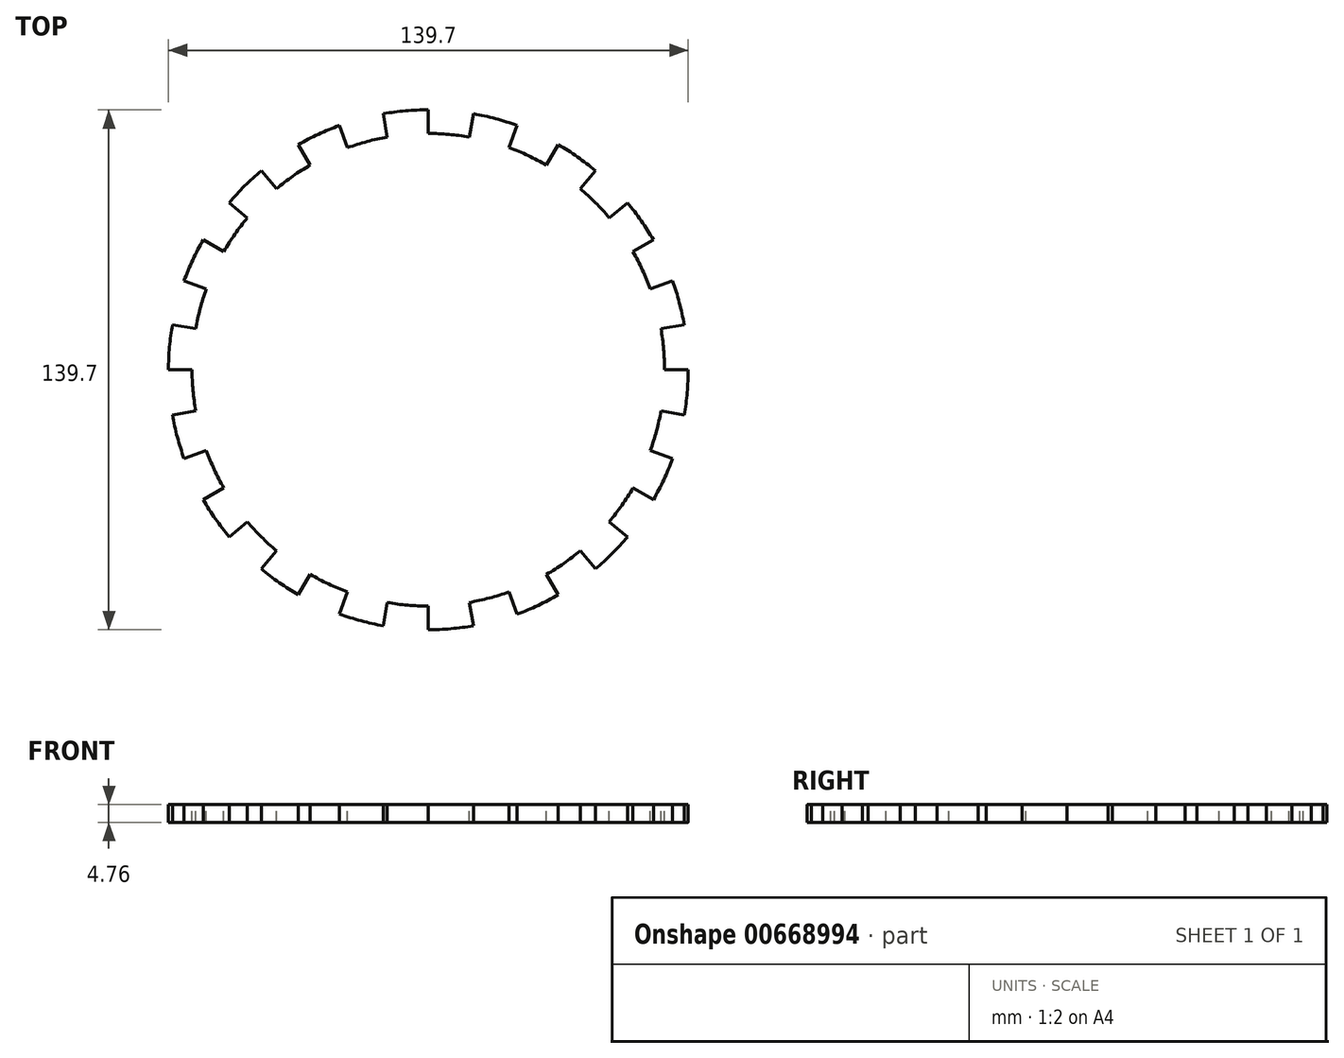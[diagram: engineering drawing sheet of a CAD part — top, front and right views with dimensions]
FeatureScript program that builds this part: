
annotation { "Feature Type Name" : "Feature", "Feature Type Description" : "" }
export const myFeature = defineFeature(function(context is Context, id is Id, definition is map)
    precondition{}
    {
        {
            var Q0;
            Q0=qCreatedBy(makeId("Top.planeOp"),FACE);
            var sketch = newSketch(context, id + "F0", { "sketchPlane" : qUnion([Q0])});
            skCircle(sketch, "E0", {"center": v(0, 0) * mm, "radius": 69.85 * mm});
            skSolve(sketch);
        }
        {
            var Q0;
            Q0 = qSketchRegion(id + "F0", true);
            extrude(context, id + "F1", {"entities" : qUnion([Q0]), "depth" : 4.76 * mm, "offsetDistance" : 25.4 * mm});
        }
        {
            var Q0;
            Q0=makeQuery(id+"F1.opExtrude","CAP_FACE",FACE,{"disambiguationData":[OSD([sQuery(id+"F0.wireOp",EDGE,"E0")])],"isStart":false});
            var sketch = newSketch(context, id + "F2", { "sketchPlane" : qUnion([Q0])});
            skLineSegment(sketch, "E1", {"start": v(0, 69.85) * mm, "end": v(0, 63.5) * mm});
            skLineSegment(sketch, "E2", {"start": v(12.13, 68.79) * mm, "end": v(11.03, 62.54) * mm});
            skArc(sketch, "E3", {"start": v(0, 63.5) * mm, "mid": v(5.53, 63.26) * mm, "end": v(11.03, 62.54) * mm});
            skArc(sketch, "E4", {"start": v(0, 69.85) * mm, "mid": v(6.09, 69.58) * mm, "end": v(12.13, 68.79) * mm});
            skArc(sketch, "E5.1.0", {"start": v(-23.9, 65.64) * mm, "mid": v(-18.08, 67.47) * mm, "end": v(-12.13, 68.79) * mm});
            skLineSegment(sketch, "E5.1.1", {"start": v(-12.13, 68.79) * mm, "end": v(-11.03, 62.54) * mm});
            skArc(sketch, "E5.1.2", {"start": v(-21.72, 59.67) * mm, "mid": v(-16.44, 61.34) * mm, "end": v(-11.03, 62.54) * mm});
            skLineSegment(sketch, "E5.1.3", {"start": v(-23.9, 65.64) * mm, "end": v(-21.72, 59.67) * mm});
            skArc(sketch, "E5.2.0", {"start": v(-44.9, 53.5) * mm, "mid": v(-40.06, 57.22) * mm, "end": v(-34.93, 60.5) * mm});
            skLineSegment(sketch, "E5.2.1", {"start": v(-34.93, 60.5) * mm, "end": v(-31.75, 55) * mm});
            skArc(sketch, "E5.2.2", {"start": v(-40.82, 48.64) * mm, "mid": v(-36.42, 52.02) * mm, "end": v(-31.75, 55) * mm});
            skLineSegment(sketch, "E5.2.3", {"start": v(-44.9, 53.5) * mm, "end": v(-40.82, 48.64) * mm});
            skArc(sketch, "E5.3.0", {"start": v(-60.5, 34.93) * mm, "mid": v(-57.22, 40.06) * mm, "end": v(-53.5, 44.9) * mm});
            skLineSegment(sketch, "E5.3.1", {"start": v(-53.5, 44.9) * mm, "end": v(-48.64, 40.82) * mm});
            skArc(sketch, "E5.3.2", {"start": v(-55, 31.75) * mm, "mid": v(-52.02, 36.42) * mm, "end": v(-48.64, 40.82) * mm});
            skLineSegment(sketch, "E5.3.3", {"start": v(-60.5, 34.93) * mm, "end": v(-55, 31.75) * mm});
            skArc(sketch, "E5.4.0", {"start": v(-68.79, 12.13) * mm, "mid": v(-67.47, 18.08) * mm, "end": v(-65.64, 23.9) * mm});
            skLineSegment(sketch, "E5.4.1", {"start": v(-65.64, 23.9) * mm, "end": v(-59.67, 21.72) * mm});
            skArc(sketch, "E5.4.2", {"start": v(-62.54, 11.03) * mm, "mid": v(-61.34, 16.44) * mm, "end": v(-59.67, 21.72) * mm});
            skLineSegment(sketch, "E5.4.3", {"start": v(-68.79, 12.13) * mm, "end": v(-62.54, 11.03) * mm});
            skArc(sketch, "E5.5.0", {"start": v(-68.79, -12.13) * mm, "mid": v(-69.58, -6.09) * mm, "end": v(-69.85, 0) * mm});
            skLineSegment(sketch, "E5.5.1", {"start": v(-69.85, 0) * mm, "end": v(-63.5, 0) * mm});
            skArc(sketch, "E5.5.2", {"start": v(-62.54, -11.03) * mm, "mid": v(-63.26, -5.53) * mm, "end": v(-63.5, 0) * mm});
            skLineSegment(sketch, "E5.5.3", {"start": v(-68.79, -12.13) * mm, "end": v(-62.54, -11.03) * mm});
            skArc(sketch, "E5.6.0", {"start": v(-60.5, -34.92) * mm, "mid": v(-63.3, -29.52) * mm, "end": v(-65.64, -23.9) * mm});
            skLineSegment(sketch, "E5.6.1", {"start": v(-65.64, -23.9) * mm, "end": v(-59.67, -21.72) * mm});
            skArc(sketch, "E5.6.2", {"start": v(-55, -31.75) * mm, "mid": v(-57.55, -26.84) * mm, "end": v(-59.67, -21.72) * mm});
            skLineSegment(sketch, "E5.6.3", {"start": v(-60.5, -34.92) * mm, "end": v(-55, -31.75) * mm});
            skArc(sketch, "E5.7.0", {"start": v(-44.9, -53.5) * mm, "mid": v(-49.4, -49.4) * mm, "end": v(-53.5, -44.9) * mm});
            skLineSegment(sketch, "E5.7.1", {"start": v(-53.5, -44.9) * mm, "end": v(-48.64, -40.82) * mm});
            skArc(sketch, "E5.7.2", {"start": v(-40.82, -48.64) * mm, "mid": v(-44.9, -44.9) * mm, "end": v(-48.64, -40.82) * mm});
            skLineSegment(sketch, "E5.7.3", {"start": v(-44.9, -53.5) * mm, "end": v(-40.82, -48.64) * mm});
            skArc(sketch, "E5.8.0", {"start": v(-23.9, -65.64) * mm, "mid": v(-29.52, -63.3) * mm, "end": v(-34.92, -60.5) * mm});
            skLineSegment(sketch, "E5.8.1", {"start": v(-34.93, -60.5) * mm, "end": v(-31.75, -55) * mm});
            skArc(sketch, "E5.8.2", {"start": v(-21.72, -59.67) * mm, "mid": v(-26.84, -57.55) * mm, "end": v(-31.75, -55) * mm});
            skLineSegment(sketch, "E5.8.3", {"start": v(-23.9, -65.64) * mm, "end": v(-21.72, -59.67) * mm});
            skArc(sketch, "E5.9.0", {"start": v(0, -69.85) * mm, "mid": v(-6.09, -69.58) * mm, "end": v(-12.13, -68.79) * mm});
            skLineSegment(sketch, "E5.9.1", {"start": v(-12.13, -68.79) * mm, "end": v(-11.03, -62.54) * mm});
            skArc(sketch, "E5.9.2", {"start": v(0, -63.5) * mm, "mid": v(-5.53, -63.26) * mm, "end": v(-11.03, -62.54) * mm});
            skLineSegment(sketch, "E5.9.3", {"start": v(0, -69.85) * mm, "end": v(0, -63.5) * mm});
            skArc(sketch, "E5.10.0", {"start": v(23.9, -65.64) * mm, "mid": v(18.08, -67.47) * mm, "end": v(12.13, -68.79) * mm});
            skLineSegment(sketch, "E5.10.1", {"start": v(12.13, -68.79) * mm, "end": v(11.03, -62.54) * mm});
            skArc(sketch, "E5.10.2", {"start": v(21.72, -59.67) * mm, "mid": v(16.44, -61.34) * mm, "end": v(11.03, -62.54) * mm});
            skLineSegment(sketch, "E5.10.3", {"start": v(23.9, -65.64) * mm, "end": v(21.72, -59.67) * mm});
            skArc(sketch, "E5.11.0", {"start": v(44.9, -53.5) * mm, "mid": v(40.06, -57.22) * mm, "end": v(34.92, -60.5) * mm});
            skLineSegment(sketch, "E5.11.1", {"start": v(34.92, -60.5) * mm, "end": v(31.75, -55) * mm});
            skArc(sketch, "E5.11.2", {"start": v(40.82, -48.64) * mm, "mid": v(36.42, -52.02) * mm, "end": v(31.75, -55) * mm});
            skLineSegment(sketch, "E5.11.3", {"start": v(44.9, -53.5) * mm, "end": v(40.82, -48.64) * mm});
            skArc(sketch, "E5.12.0", {"start": v(60.5, -34.93) * mm, "mid": v(57.22, -40.06) * mm, "end": v(53.5, -44.9) * mm});
            skLineSegment(sketch, "E5.12.1", {"start": v(53.5, -44.9) * mm, "end": v(48.64, -40.82) * mm});
            skArc(sketch, "E5.12.2", {"start": v(55, -31.75) * mm, "mid": v(52.02, -36.42) * mm, "end": v(48.64, -40.82) * mm});
            skLineSegment(sketch, "E5.12.3", {"start": v(60.5, -34.93) * mm, "end": v(55, -31.75) * mm});
            skArc(sketch, "E5.13.0", {"start": v(68.79, -12.13) * mm, "mid": v(67.47, -18.08) * mm, "end": v(65.64, -23.9) * mm});
            skLineSegment(sketch, "E5.13.1", {"start": v(65.64, -23.9) * mm, "end": v(59.67, -21.72) * mm});
            skArc(sketch, "E5.13.2", {"start": v(62.54, -11.03) * mm, "mid": v(61.34, -16.44) * mm, "end": v(59.67, -21.72) * mm});
            skLineSegment(sketch, "E5.13.3", {"start": v(68.79, -12.13) * mm, "end": v(62.54, -11.03) * mm});
            skArc(sketch, "E5.14.0", {"start": v(68.79, 12.13) * mm, "mid": v(69.58, 6.09) * mm, "end": v(69.85, 0) * mm});
            skLineSegment(sketch, "E5.14.1", {"start": v(69.85, 0) * mm, "end": v(63.5, 0) * mm});
            skArc(sketch, "E5.14.2", {"start": v(62.54, 11.03) * mm, "mid": v(63.26, 5.53) * mm, "end": v(63.5, 0) * mm});
            skLineSegment(sketch, "E5.14.3", {"start": v(68.79, 12.13) * mm, "end": v(62.54, 11.03) * mm});
            skArc(sketch, "E5.15.0", {"start": v(60.5, 34.92) * mm, "mid": v(63.3, 29.52) * mm, "end": v(65.64, 23.9) * mm});
            skLineSegment(sketch, "E5.15.1", {"start": v(65.64, 23.9) * mm, "end": v(59.67, 21.72) * mm});
            skArc(sketch, "E5.15.2", {"start": v(55, 31.75) * mm, "mid": v(57.55, 26.84) * mm, "end": v(59.67, 21.72) * mm});
            skLineSegment(sketch, "E5.15.3", {"start": v(60.5, 34.92) * mm, "end": v(55, 31.75) * mm});
            skArc(sketch, "E5.16.0", {"start": v(44.9, 53.5) * mm, "mid": v(49.4, 49.4) * mm, "end": v(53.5, 44.9) * mm});
            skLineSegment(sketch, "E5.16.1", {"start": v(53.5, 44.9) * mm, "end": v(48.64, 40.82) * mm});
            skArc(sketch, "E5.16.2", {"start": v(40.82, 48.64) * mm, "mid": v(44.9, 44.9) * mm, "end": v(48.64, 40.82) * mm});
            skLineSegment(sketch, "E5.16.3", {"start": v(44.9, 53.5) * mm, "end": v(40.82, 48.64) * mm});
            skArc(sketch, "E5.17.0", {"start": v(23.9, 65.64) * mm, "mid": v(29.52, 63.3) * mm, "end": v(34.92, 60.5) * mm});
            skLineSegment(sketch, "E5.17.1", {"start": v(34.92, 60.5) * mm, "end": v(31.75, 55) * mm});
            skArc(sketch, "E5.17.2", {"start": v(21.72, 59.67) * mm, "mid": v(26.84, 57.55) * mm, "end": v(31.75, 55) * mm});
            skLineSegment(sketch, "E5.17.3", {"start": v(23.9, 65.64) * mm, "end": v(21.72, 59.67) * mm});
            skSolve(sketch);
        }
        {
            var Q0;
            Q0 = qSketchRegion(id + "F2", true);
            extrude(context, id + "F3", {"entities" : qUnion([Q0]), "operationType" : NewBodyOperationType.REMOVE, "oppositeDirection" : true, "depth" : 25.4 * mm, "offsetDistance" : 25.4 * mm});
        }
    });
